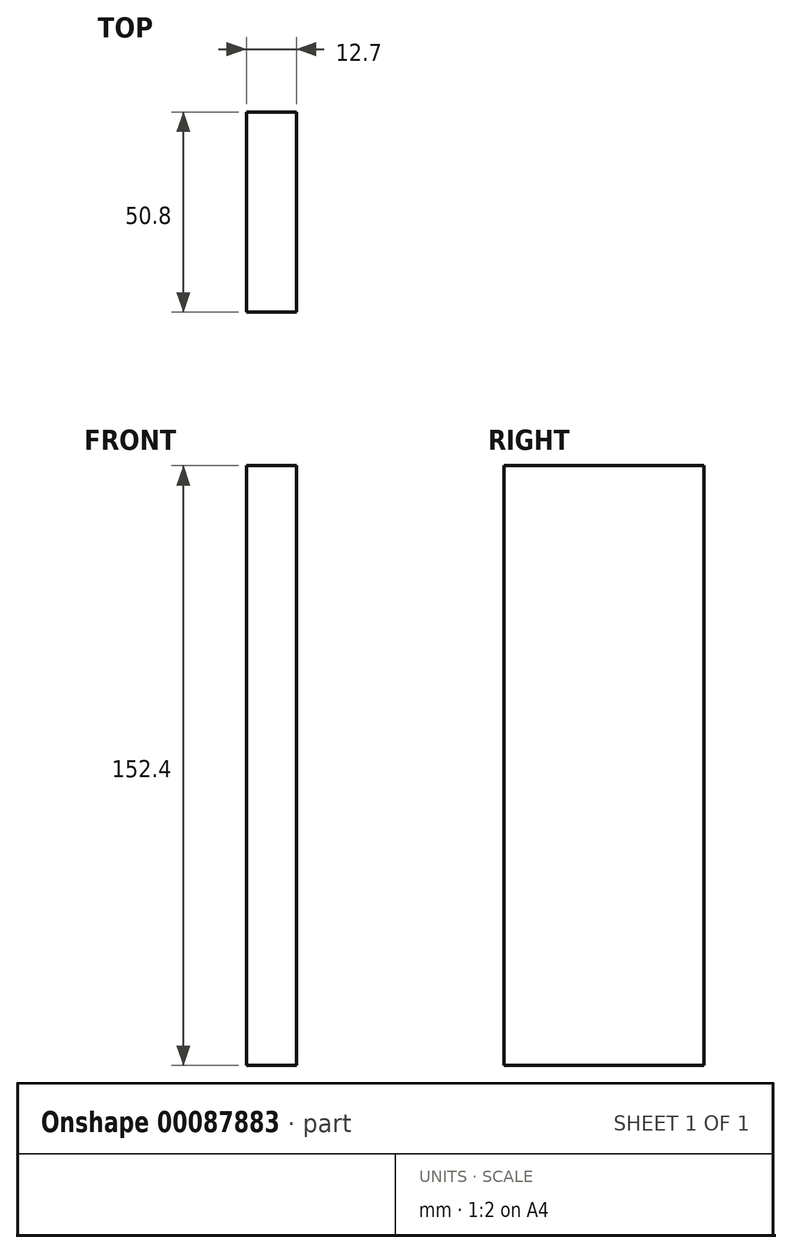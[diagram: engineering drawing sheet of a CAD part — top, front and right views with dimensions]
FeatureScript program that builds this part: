
annotation { "Feature Type Name" : "Feature", "Feature Type Description" : "" }
export const myFeature = defineFeature(function(context is Context, id is Id, definition is map)
    precondition{}
    {
        {
            var Q0;
            Q0=qCreatedBy(makeId("Front.planeOp"),FACE);
            var sketch = newSketch(context, id + "F0", { "sketchPlane" : qUnion([Q0])});
            skLineSegment(sketch, "E0.bottom", {"start": v(-50.59, 138.43) * mm, "end": v(-37.89, 138.43) * mm});
            skLineSegment(sketch, "E0.top", {"start": v(-50.59, -13.97) * mm, "end": v(-37.89, -13.97) * mm});
            skLineSegment(sketch, "E0.left", {"start": v(-50.59, 138.43) * mm, "end": v(-50.59, -13.97) * mm});
            skLineSegment(sketch, "E0.right", {"start": v(-37.89, 138.43) * mm, "end": v(-37.89, -13.97) * mm});
            skSolve(sketch);
        }
        {
            var Q0;
            Q0 = qSketchRegion(id + "F0", true);
            extrude(context, id + "F1", {"entities" : qUnion([Q0]), "depth" : 50.8 * mm});
        }
    });
